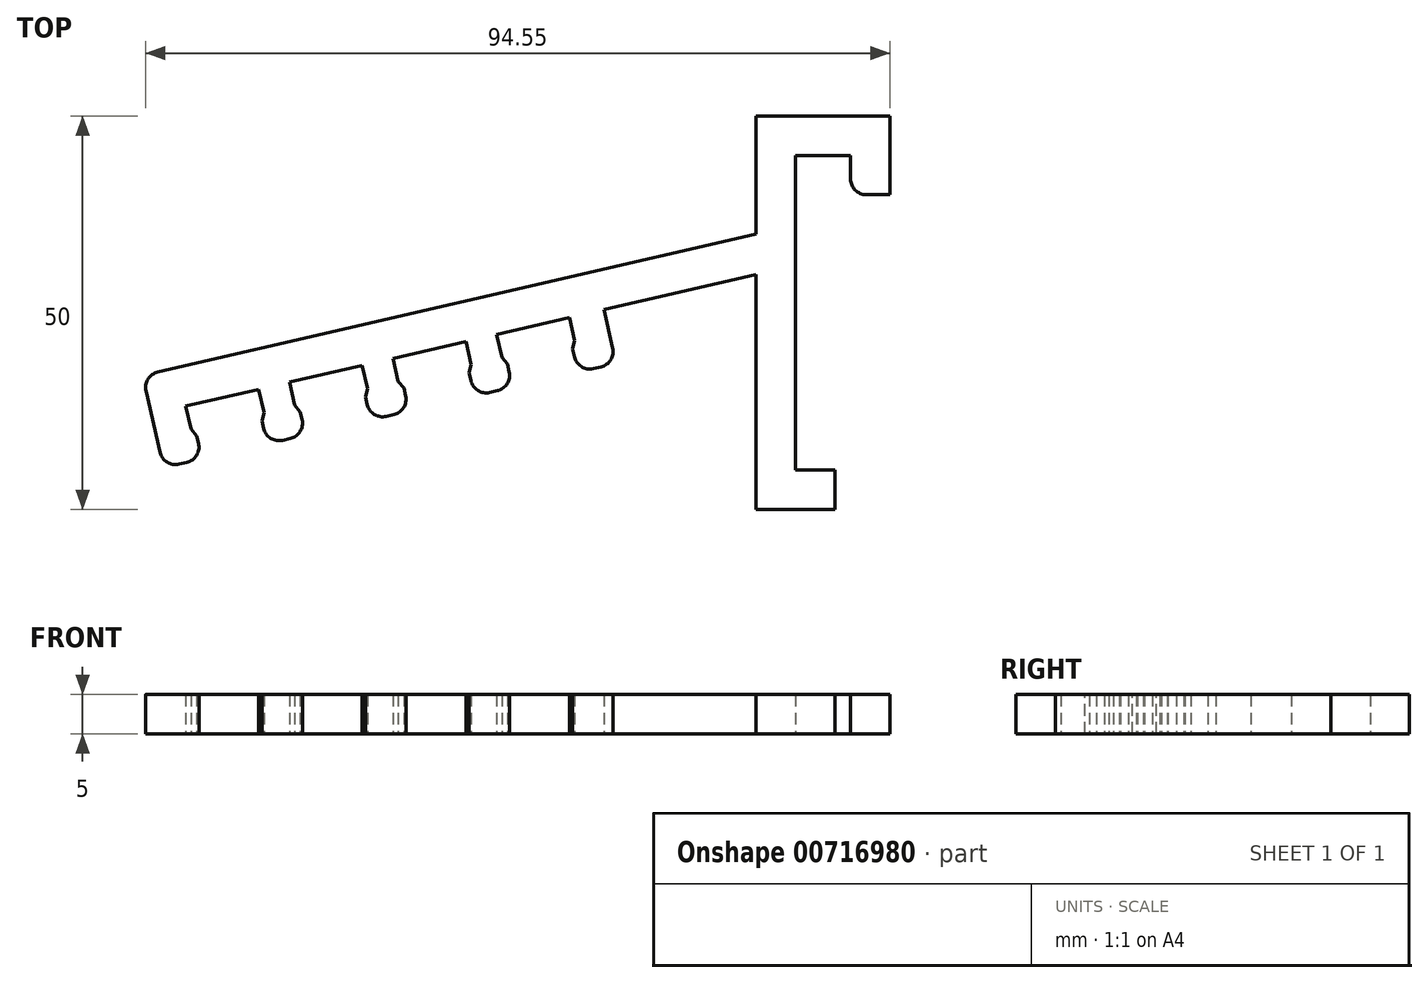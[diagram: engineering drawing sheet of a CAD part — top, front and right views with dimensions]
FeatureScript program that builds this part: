
annotation { "Feature Type Name" : "Feature", "Feature Type Description" : "" }
export const myFeature = defineFeature(function(context is Context, id is Id, definition is map)
    precondition{}
    {
        {
            var Q0;
            Q0=qCreatedBy(makeId("Top.planeOp"),FACE);
            var sketch = newSketch(context, id + "F0", { "sketchPlane" : qUnion([Q0])});
            skLineSegment(sketch, "E0.bottom", {"start": v(2.5, 25) * mm, "end": v(-2.5, 25) * mm});
            skLineSegment(sketch, "E0.top", {"start": v(2.5, -25) * mm, "end": v(-2.5, -25) * mm});
            skLineSegment(sketch, "E0.left", {"start": v(2.5, 25) * mm, "end": v(2.5, -25) * mm});
            skLineSegment(sketch, "E0.right", {"start": v(-2.5, 25) * mm, "end": v(-2.5, -25) * mm});
            skPoint(sketch, "E0.middle", {"position": v(0, 0) * mm});
            skLineSegment(sketch, "E1.bottom", {"start": v(2.5, 25) * mm, "end": v(14.5, 25) * mm});
            skLineSegment(sketch, "E1.top", {"start": v(2.5, 20) * mm, "end": v(14.5, 20) * mm});
            skLineSegment(sketch, "E1.left", {"start": v(2.5, 25) * mm, "end": v(2.5, 20) * mm});
            skLineSegment(sketch, "E1.right", {"start": v(14.5, 25) * mm, "end": v(14.5, 20) * mm});
            skLineSegment(sketch, "E2.bottom", {"start": v(14.5, 20) * mm, "end": v(9.5, 20) * mm});
            skLineSegment(sketch, "E2.top", {"start": v(14.5, 15) * mm, "end": v(9.5, 15) * mm});
            skLineSegment(sketch, "E2.left", {"start": v(14.5, 20) * mm, "end": v(14.5, 15) * mm});
            skLineSegment(sketch, "E2.right", {"start": v(9.5, 20) * mm, "end": v(9.5, 15) * mm});
            skLineSegment(sketch, "E3.bottom", {"start": v(2.5, -25) * mm, "end": v(7.5, -25) * mm});
            skLineSegment(sketch, "E3.top", {"start": v(2.5, -20) * mm, "end": v(7.5, -20) * mm});
            skLineSegment(sketch, "E3.left", {"start": v(2.5, -25) * mm, "end": v(2.5, -20) * mm});
            skLineSegment(sketch, "E3.right", {"start": v(7.5, -25) * mm, "end": v(7.5, -20) * mm});
            skLineSegment(sketch, "E4", {"start": v(-2.5, 10) * mm, "end": v(-80.45, -8) * mm});
            skLineSegment(sketch, "E5", {"start": v(-80.45, -8) * mm, "end": v(-79.32, -12.87) * mm});
            skLineSegment(sketch, "E6", {"start": v(-79.32, -12.87) * mm, "end": v(-2.5, 4.87) * mm});
            skLineSegment(sketch, "E7", {"start": v(-79.32, -12.87) * mm, "end": v(-77.75, -19.69) * mm});
            skLineSegment(sketch, "E8", {"start": v(-77.75, -19.69) * mm, "end": v(-72.88, -18.56) * mm});
            skLineSegment(sketch, "E9", {"start": v(-72.88, -18.56) * mm, "end": v(-73.55, -15.64) * mm});
            skLineSegment(sketch, "E10", {"start": v(-74.94, -11.86) * mm, "end": v(-74.27, -14.78) * mm});
            skLineSegment(sketch, "E11", {"start": v(-74.27, -14.78) * mm, "end": v(-73.55, -15.64) * mm});
            skLineSegment(sketch, "E12", {"start": v(-65.68, -9.72) * mm, "end": v(-65, -12.64) * mm});
            skLineSegment(sketch, "E13", {"start": v(-61.79, -8.82) * mm, "end": v(-61.11, -11.74) * mm});
            skLineSegment(sketch, "E14", {"start": v(-77.75, -19.69) * mm, "end": v(-1.55, -2.1) * mm, "construction": true});
            skLineSegment(sketch, "E15", {"start": v(-64.6, -16.65) * mm, "end": v(-65.27, -13.73) * mm});
            skLineSegment(sketch, "E16", {"start": v(-65.27, -13.73) * mm, "end": v(-65, -12.64) * mm});
            skLineSegment(sketch, "E17", {"start": v(-64.6, -16.65) * mm, "end": v(-59.72, -15.53) * mm});
            skLineSegment(sketch, "E18", {"start": v(-59.72, -15.53) * mm, "end": v(-60.4, -12.6) * mm});
            skLineSegment(sketch, "E19", {"start": v(-60.4, -12.6) * mm, "end": v(-61.11, -11.74) * mm});
            skLineSegment(sketch, "E20", {"start": v(-52.53, -6.68) * mm, "end": v(-51.85, -9.6) * mm});
            skLineSegment(sketch, "E21", {"start": v(-51.85, -9.6) * mm, "end": v(-52.12, -10.7) * mm});
            skLineSegment(sketch, "E22", {"start": v(-52.12, -10.7) * mm, "end": v(-51.44, -13.61) * mm});
            skLineSegment(sketch, "E23", {"start": v(-51.44, -13.61) * mm, "end": v(-46.57, -12.5) * mm});
            skLineSegment(sketch, "E24", {"start": v(-46.57, -12.5) * mm, "end": v(-47.25, -9.57) * mm});
            skLineSegment(sketch, "E25", {"start": v(-48.63, -5.78) * mm, "end": v(-47.96, -8.7) * mm});
            skLineSegment(sketch, "E26", {"start": v(-47.96, -8.7) * mm, "end": v(-47.25, -9.57) * mm});
            skLineSegment(sketch, "E27", {"start": v(-38.29, -10.58) * mm, "end": v(-33.42, -9.45) * mm});
            skLineSegment(sketch, "E28", {"start": v(-33.42, -9.45) * mm, "end": v(-34.1, -6.53) * mm});
            skLineSegment(sketch, "E29", {"start": v(-38.29, -10.58) * mm, "end": v(-38.96, -7.65) * mm});
            skLineSegment(sketch, "E30", {"start": v(-39.38, -3.64) * mm, "end": v(-38.7, -6.57) * mm});
            skLineSegment(sketch, "E31", {"start": v(-38.7, -6.57) * mm, "end": v(-38.96, -7.65) * mm});
            skLineSegment(sketch, "E32", {"start": v(-35.48, -2.75) * mm, "end": v(-34.8, -5.67) * mm});
            skLineSegment(sketch, "E33", {"start": v(-34.8, -5.67) * mm, "end": v(-34.1, -6.53) * mm});
            skLineSegment(sketch, "E34", {"start": v(-26.22, -0.6) * mm, "end": v(-25.55, -3.53) * mm});
            skLineSegment(sketch, "E35", {"start": v(-25.13, -7.54) * mm, "end": v(-25.8, -4.62) * mm});
            skLineSegment(sketch, "E36", {"start": v(-25.8, -4.62) * mm, "end": v(-25.55, -3.53) * mm});
            skLineSegment(sketch, "E37", {"start": v(-25.13, -7.54) * mm, "end": v(-20.26, -6.42) * mm});
            skLineSegment(sketch, "E38", {"start": v(-20.26, -6.42) * mm, "end": v(-21.84, 0.4) * mm});
            skLineSegment(sketch, "E39", {"start": v(7.5, -20) * mm, "end": v(-113.43, -20) * mm, "construction": true});
            skSolve(sketch);
        }
        {
            var Q0;
            Q0 = qSketchRegion(id + "F0", true);
            extrude(context, id + "F1", {"entities" : qUnion([Q0]), "depth" : 5 * mm, "offsetDistance" : 25 * mm});
        }
        {
            var Q0;
            Q0=makeQuery(id+"F1.opExtrude","SWEPT_EDGE",EDGE,{"disambiguationData":[OSD([sQuery(id+"F0.wireOp",EDGE,"E8"),sQuery(id+"F0.wireOp",EDGE,"E9")])]});
            var Q1;
            Q1=makeQuery(id+"F1.opExtrude","SWEPT_EDGE",EDGE,{"disambiguationData":[OSD([sQuery(id+"F0.wireOp",EDGE,"E15"),sQuery(id+"F0.wireOp",EDGE,"E17")])]});
            var Q2;
            Q2=makeQuery(id+"F1.opExtrude","SWEPT_EDGE",EDGE,{"disambiguationData":[OSD([sQuery(id+"F0.wireOp",EDGE,"E17"),sQuery(id+"F0.wireOp",EDGE,"E18")])]});
            var Q3;
            Q3=makeQuery(id+"F1.opExtrude","SWEPT_EDGE",EDGE,{"disambiguationData":[OSD([sQuery(id+"F0.wireOp",EDGE,"E22"),sQuery(id+"F0.wireOp",EDGE,"E23")])]});
            var Q4;
            Q4=makeQuery(id+"F1.opExtrude","SWEPT_EDGE",EDGE,{"disambiguationData":[OSD([sQuery(id+"F0.wireOp",EDGE,"E23"),sQuery(id+"F0.wireOp",EDGE,"E24")])]});
            var Q5;
            Q5=makeQuery(id+"F1.opExtrude","SWEPT_EDGE",EDGE,{"disambiguationData":[OSD([sQuery(id+"F0.wireOp",EDGE,"E27"),sQuery(id+"F0.wireOp",EDGE,"E29")])]});
            var Q6;
            Q6=makeQuery(id+"F1.opExtrude","SWEPT_EDGE",EDGE,{"disambiguationData":[OSD([sQuery(id+"F0.wireOp",EDGE,"E27"),sQuery(id+"F0.wireOp",EDGE,"E28")])]});
            var Q7;
            Q7=makeQuery(id+"F1.opExtrude","SWEPT_EDGE",EDGE,{"disambiguationData":[OSD([sQuery(id+"F0.wireOp",EDGE,"E35"),sQuery(id+"F0.wireOp",EDGE,"E37")])]});
            var Q8;
            Q8=makeQuery(id+"F1.opExtrude","SWEPT_EDGE",EDGE,{"disambiguationData":[OSD([sQuery(id+"F0.wireOp",EDGE,"E7"),sQuery(id+"F0.wireOp",EDGE,"E8")])]});
            var Q9;
            Q9=makeQuery(id+"F1.opExtrude","SWEPT_EDGE",EDGE,{"disambiguationData":[OSD([sQuery(id+"F0.wireOp",EDGE,"E4"),sQuery(id+"F0.wireOp",EDGE,"E5")])]});
            var Q10;
            Q10=makeQuery(id+"F1.opExtrude","SWEPT_EDGE",EDGE,{"disambiguationData":[OSD([sQuery(id+"F0.wireOp",EDGE,"E37"),sQuery(id+"F0.wireOp",EDGE,"E38")])]});
            var Q11;
            Q11=makeQuery(id+"F1.opExtrude","SWEPT_EDGE",EDGE,{"disambiguationData":[OSD([sQuery(id+"F0.wireOp",EDGE,"E2.top"),sQuery(id+"F0.wireOp",EDGE,"E2.right")])]});
            fillet(context, id + "F2", {"entities" : qUnion([Q0, Q1, Q2, Q3, Q4, Q5, Q6, Q7, Q8, Q9, Q10, Q11]), "radius" : 2 * mm, "tangentPropagation" : true, "allowEdgeOverflow" : false});
        }
    });
